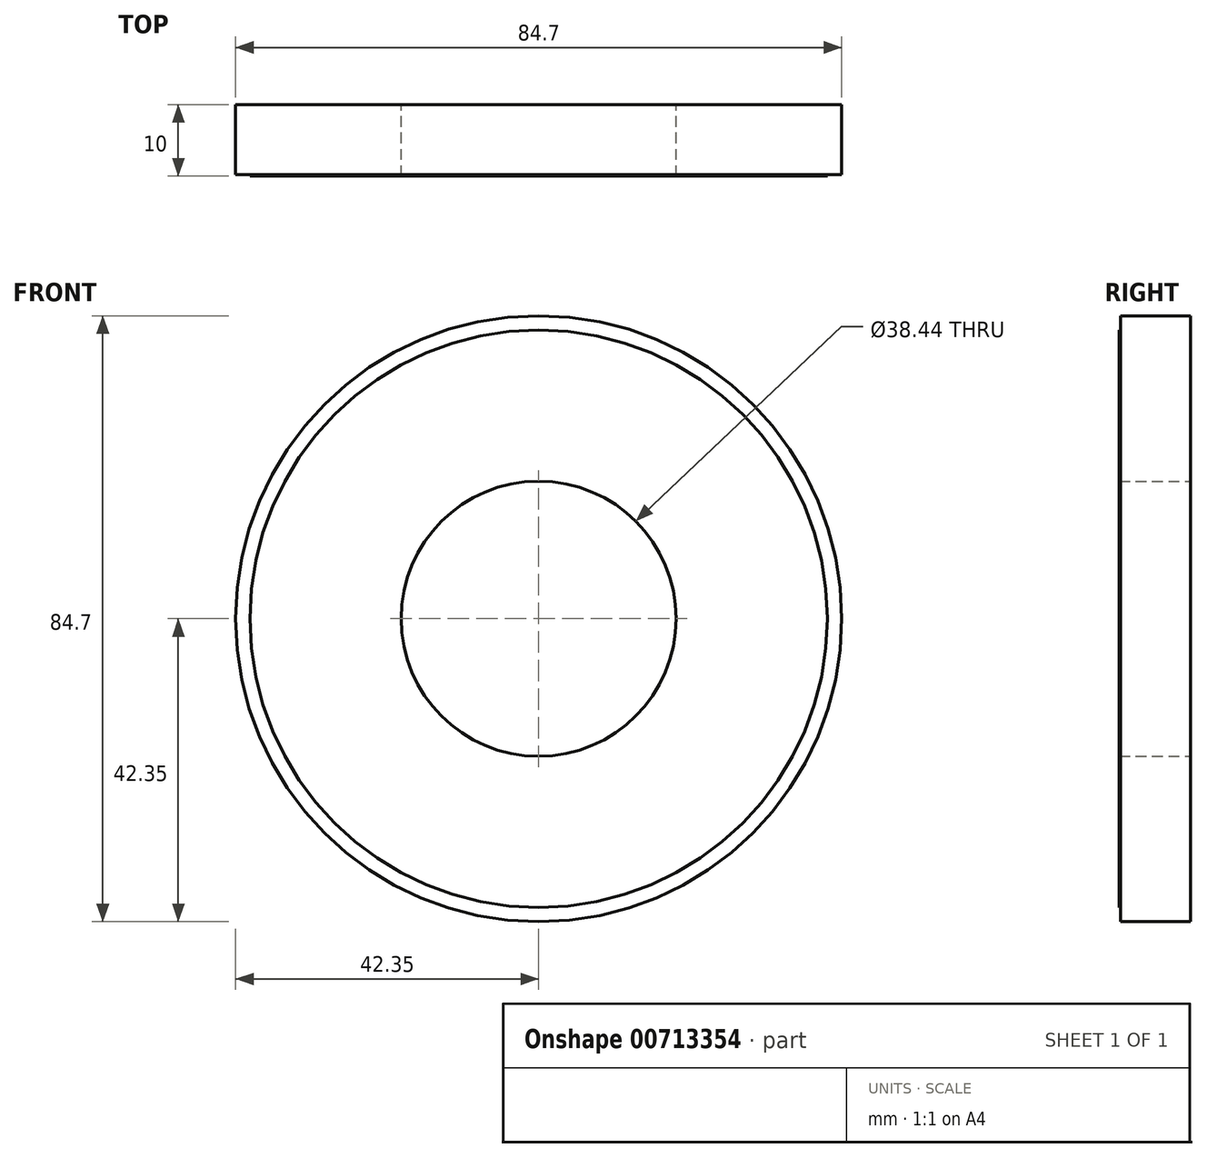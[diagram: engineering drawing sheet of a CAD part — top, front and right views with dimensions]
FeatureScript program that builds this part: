
annotation { "Feature Type Name" : "Feature", "Feature Type Description" : "" }
export const myFeature = defineFeature(function(context is Context, id is Id, definition is map)
    precondition{}
    {
        {
            var Q0;
            Q0=qCreatedBy(makeId("Front.planeOp"),FACE);
            var sketch = newSketch(context, id + "F0", { "sketchPlane" : qUnion([Q0])});
            skCircle(sketch, "E0", {"center": v(0, 0) * mm, "radius": 42.35 * mm});
            skCircle(sketch, "E1.0", {"center": v(0, 0) * mm, "radius": 40.35 * mm});
            skCircle(sketch, "E2", {"center": v(0, 0) * mm, "radius": 19.22 * mm});
            skSolve(sketch);
        }
        {
            var Q0;
            Q0=makeQuery(id+"F0.imprint","IMPRINT",FACE,{"disambiguationData":[TD([[makeQuery(id+"F0.imprint","IMPRINT",EDGE,{"derivedFrom":sQuery(id+"F0.wireOp",EDGE,"E1.0")}),1.0]])]});
            extrude(context, id + "F1", {"entities" : qUnion([Q0]), "endBound" : BoundingType.SYMMETRIC, "depth" : 10 * mm, "offsetDistance" : 25 * mm});
        }
        {
            var Q0;
            Q0=makeQuery(id+"F0.imprint","IMPRINT",FACE,{"disambiguationData":[TD([[makeQuery(id+"F0.imprint","IMPRINT",EDGE,{"derivedFrom":sQuery(id+"F0.wireOp",EDGE,"E0")}),1.0]])]});
            extrude(context, id + "F2", {"entities" : qUnion([Q0]), "operationType" : NewBodyOperationType.ADD, "depth" : 4.8 * mm, "offsetDistance" : 25 * mm, "hasSecondDirection" : true, "secondDirectionOppositeDirection" : true, "secondDirectionDepth" : 5 * mm});
        }
    });
